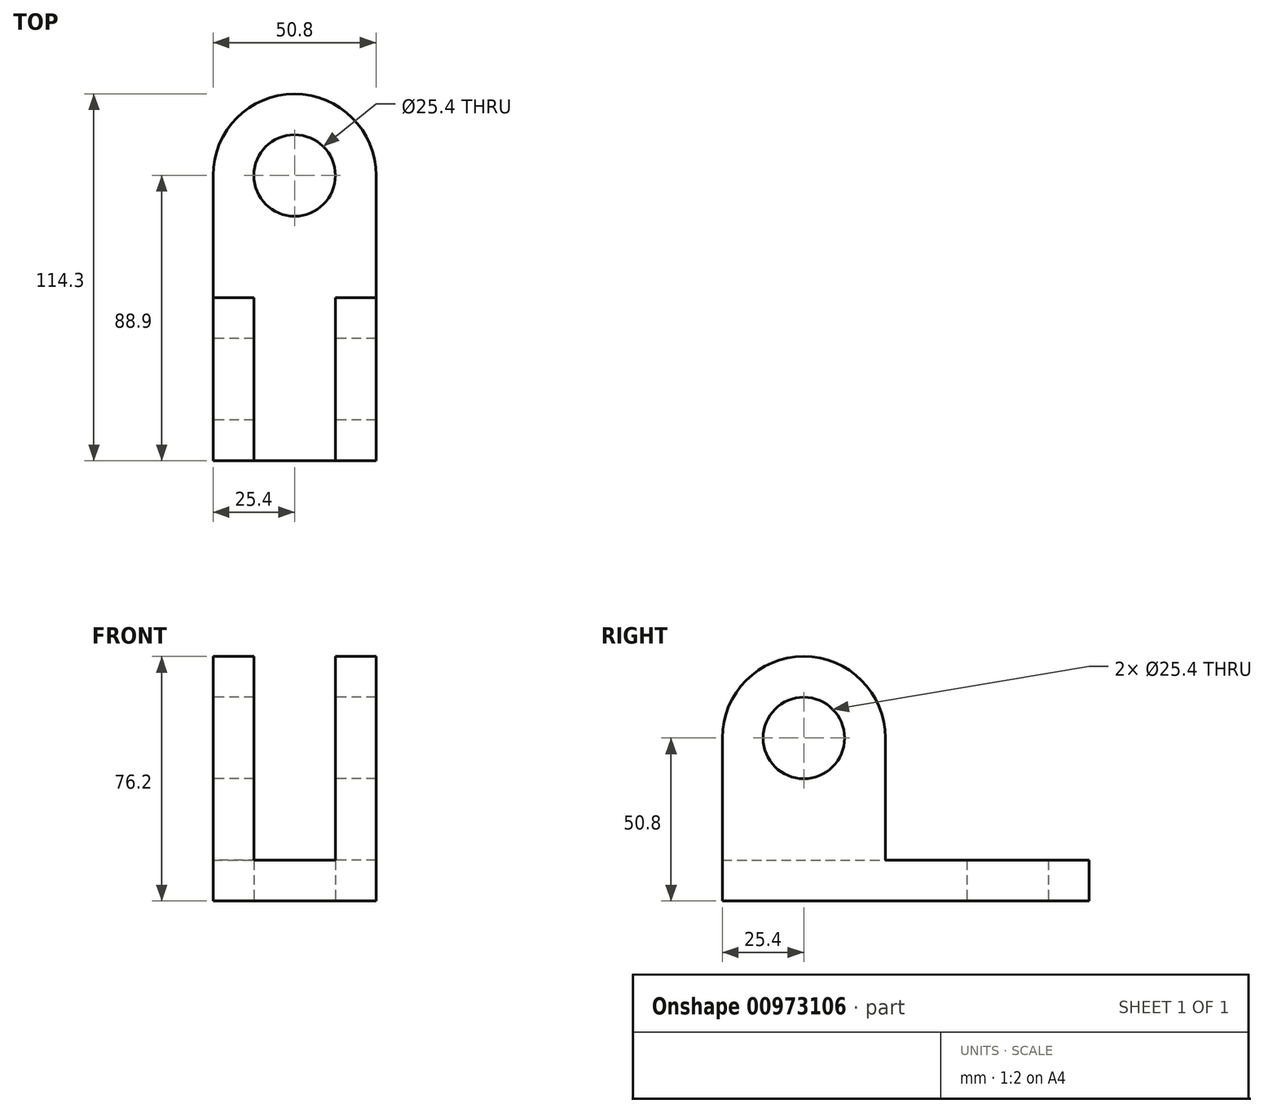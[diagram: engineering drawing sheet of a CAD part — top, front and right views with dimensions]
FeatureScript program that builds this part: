
annotation { "Feature Type Name" : "Feature", "Feature Type Description" : "" }
export const myFeature = defineFeature(function(context is Context, id is Id, definition is map)
    precondition{}
    {
        {
            var Q0;
            Q0=qCreatedBy(makeId("Top.planeOp"),FACE);
            var sketch = newSketch(context, id + "F0", { "sketchPlane" : qUnion([Q0])});
            skLineSegment(sketch, "E0.bottom", {"start": v(0, 0) * mm, "end": v(50.8, 0) * mm});
            skLineSegment(sketch, "E0.top", {"start": v(25.4, 114.3) * mm, "end": v(25.4, 114.3) * mm});
            skLineSegment(sketch, "E0.left", {"start": v(0, 0) * mm, "end": v(0, 88.9) * mm});
            skLineSegment(sketch, "E0.right", {"start": v(50.8, 0) * mm, "end": v(50.8, 88.9) * mm});
            skPoint(sketch, "E1.visualSharp", {"position": v(0, 114.3) * mm});
            skArc(sketch, "E1.filletArc", {"start": v(25.4, 114.3) * mm, "mid": v(7.44, 106.86) * mm, "end": v(0, 88.9) * mm});
            skPoint(sketch, "E2.visualSharp", {"position": v(50.8, 114.3) * mm});
            skArc(sketch, "E2.filletArc", {"start": v(50.8, 88.9) * mm, "mid": v(43.36, 106.86) * mm, "end": v(25.4, 114.3) * mm});
            skCircle(sketch, "E3", {"center": v(25.4, 88.9) * mm, "radius": 12.7 * mm});
            skSolve(sketch);
        }
        {
            var Q0;
            Q0=makeQuery(id+"F0.imprint","IMPRINT",FACE,{"disambiguationData":[TD([[makeQuery(id+"F0.imprint","IMPRINT",EDGE,{"derivedFrom":sQuery(id+"F0.wireOp",EDGE,"E0.bottom")}),1.0]])]});
            extrude(context, id + "F1", {"entities" : qUnion([Q0]), "depth" : 12.7 * mm, "offsetDistance" : 25.4 * mm});
        }
        {
            var Q0;
            Q0=makeQuery(id+"F1.opExtrude","CAP_FACE",FACE,{"disambiguationData":[OSD([sQuery(id+"F0.wireOp",EDGE,"E0.bottom"),sQuery(id+"F0.wireOp",EDGE,"E0.left"),sQuery(id+"F0.wireOp",EDGE,"E0.right"),sQuery(id+"F0.wireOp",EDGE,"E1.filletArc"),sQuery(id+"F0.wireOp",EDGE,"E2.filletArc"),sQuery(id+"F0.wireOp",EDGE,"E3")])],"isStart":false});
            var sketch = newSketch(context, id + "F2", { "sketchPlane" : qUnion([Q0])});
            skLineSegment(sketch, "E4.bottom", {"start": v(0, 0) * mm, "end": v(12.7, 0) * mm});
            skLineSegment(sketch, "E4.top", {"start": v(0, 50.8) * mm, "end": v(12.7, 50.8) * mm});
            skLineSegment(sketch, "E4.left", {"start": v(0, 0) * mm, "end": v(0, 50.8) * mm});
            skLineSegment(sketch, "E4.right", {"start": v(12.7, 0) * mm, "end": v(12.7, 50.8) * mm});
            skLineSegment(sketch, "E5.bottom", {"start": v(50.8, 0) * mm, "end": v(38.1, 0) * mm});
            skLineSegment(sketch, "E5.top", {"start": v(50.8, 50.8) * mm, "end": v(38.1, 50.8) * mm});
            skLineSegment(sketch, "E5.left", {"start": v(50.8, 0) * mm, "end": v(50.8, 50.8) * mm});
            skLineSegment(sketch, "E5.right", {"start": v(38.1, 0) * mm, "end": v(38.1, 50.8) * mm});
            skSolve(sketch);
        }
        {
            var Q0;
            Q0=makeQuery(id+"F2.imprint","IMPRINT",FACE,{"disambiguationData":[TD([[makeQuery(id+"F2.imprint","IMPRINT",EDGE,{"derivedFrom":sQuery(id+"F2.wireOp",EDGE,"E4.bottom")}),1.0]])]});
            var Q1;
            Q1=makeQuery(id+"F2.imprint","IMPRINT",FACE,{"disambiguationData":[TD([[makeQuery(id+"F2.imprint","IMPRINT",EDGE,{"derivedFrom":sQuery(id+"F2.wireOp",EDGE,"E5.bottom")}),1.0]])]});
            extrude(context, id + "F3", {"entities" : qUnion([Q0, Q1]), "operationType" : NewBodyOperationType.ADD, "depth" : 63.5 * mm, "offsetDistance" : 25.4 * mm});
        }
        {
            var Q0;
            Q0=makeQuery(id+"F3.opExtrude","CAP_EDGE",EDGE,{"disambiguationData":[OSD([sQuery(id+"F2.wireOp",EDGE,"E4.top")])],"isStart":false});
            var Q1;
            Q1=makeQuery(id+"F3.opExtrude","CAP_EDGE",EDGE,{"disambiguationData":[OSD([sQuery(id+"F2.wireOp",EDGE,"E4.bottom")])],"isStart":false});
            var Q2;
            Q2=makeQuery(id+"F3.opExtrude","CAP_EDGE",EDGE,{"disambiguationData":[OSD([sQuery(id+"F2.wireOp",EDGE,"E5.bottom")])],"isStart":false});
            var Q3;
            Q3=makeQuery(id+"F3.opExtrude","CAP_EDGE",EDGE,{"disambiguationData":[OSD([sQuery(id+"F2.wireOp",EDGE,"E5.top")])],"isStart":false});
            fillet(context, id + "F4", {"entities" : qUnion([Q0, Q1, Q2, Q3]), "radius" : 25.4 * mm, "tangentPropagation" : true, "allowEdgeOverflow" : false});
        }
        {
            var Q0;
            Q0=makeQuery(id+"F3.boolean.opBoolean","MERGE",FACE,{"derivedFrom":[makeQuery(id+"F1.opExtrude","SWEPT_FACE",FACE,{"disambiguationData":[OSD([sQuery(id+"F0.wireOp",EDGE,"E0.left")])]}),makeQuery(id+"F3.opExtrude","SWEPT_FACE",FACE,{"disambiguationData":[OSD([sQuery(id+"F2.wireOp",EDGE,"E4.left")])]})]});
            var sketch = newSketch(context, id + "F5", { "sketchPlane" : qUnion([Q0])});
            skLineSegment(sketch, "E6", {"start": v(-25.4, 76.2) * mm, "end": v(-25.4, 0) * mm, "construction": true});
            skLineSegment(sketch, "E7", {"start": v(0, 50.8) * mm, "end": v(-50.8, 50.8) * mm, "construction": true});
            skCircle(sketch, "E8", {"center": v(-25.4, 50.8) * mm, "radius": 12.7 * mm});
            skSolve(sketch);
        }
        {
            var Q0;
            Q0=sQuery(id+"F5.wireOp",VERTEX,"E8.center");
            var Q1;
            Q1=makeQuery(id+"F1.opExtrude","SWEPT_BODY",BODY,{"disambiguationData":[OSD([sQuery(id+"F0.wireOp",EDGE,"E0.bottom"),sQuery(id+"F0.wireOp",EDGE,"E0.left"),sQuery(id+"F0.wireOp",EDGE,"E0.right"),sQuery(id+"F0.wireOp",EDGE,"E1.filletArc"),sQuery(id+"F0.wireOp",EDGE,"E2.filletArc"),sQuery(id+"F0.wireOp",EDGE,"E3")])]});
            hole(context, id + "F6", {"style" : HoleStyle.SIMPLE, "endStyle" : HoleEndStyle.THROUGH, "holeDiameter" : 25.4 * mm, "majorDiameter" : 6.35 * mm, "isTappedThrough" : true, "tappedDepth" : 12.7 * mm, "tapClearance" : 3, "locations" : qUnion([Q0]), "scope" : qUnion([Q1])});
        }
    });
